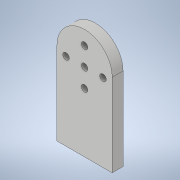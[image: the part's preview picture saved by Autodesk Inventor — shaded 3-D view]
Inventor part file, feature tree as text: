
AUTODESK INVENTOR PART (.ipt)
format: ipt  version: 2022 (Build 260153000, 153)  size: 138,752 bytes
history: native  units: mm
features: sketch x3, extrude x2, hole x1, fillet x1
ambient origin geometry x8: Origin, YZ Plane, XZ Plane, XY Plane, X Axis, Y Axis, Z Axis, Center Point
bodies: Solid1 (feature_tree)
feature tree (7):
  extrude  "Extrusion1"  Depth=25.4mm
  extrude  "Extrusion2"  Depth=5.0mm
  hole  "Hole1"  [1 undecoded]
  fillet  "Fillet1"  Radius=3.0mm
  sketch  "Sketch1"  dims[d0=25.4mm d1=50.8mm]
  sketch  "Sketch2"  dims[d2=5.0mm d3=0.0mm d4=24.6mm]
  sketch  "Sketch3"  dims[d5=17.0mm d6=3.0mm d7=3.0mm d8=40.0mm d10=360.0deg d12=15.0mm d13=5.0mm d14=0.0mm d15=2.5mm d16=2.46mm d17=6.0mm d18=4.0mm d19=2.0mm d20=90.0deg d21=13.6906mm d22=20.594885mm]
note: 1 required parameter value undecoded (feature->parameter linkage not recoverable at this tier; creation-order binding heuristic only, values carry confidence <= 0.55)
